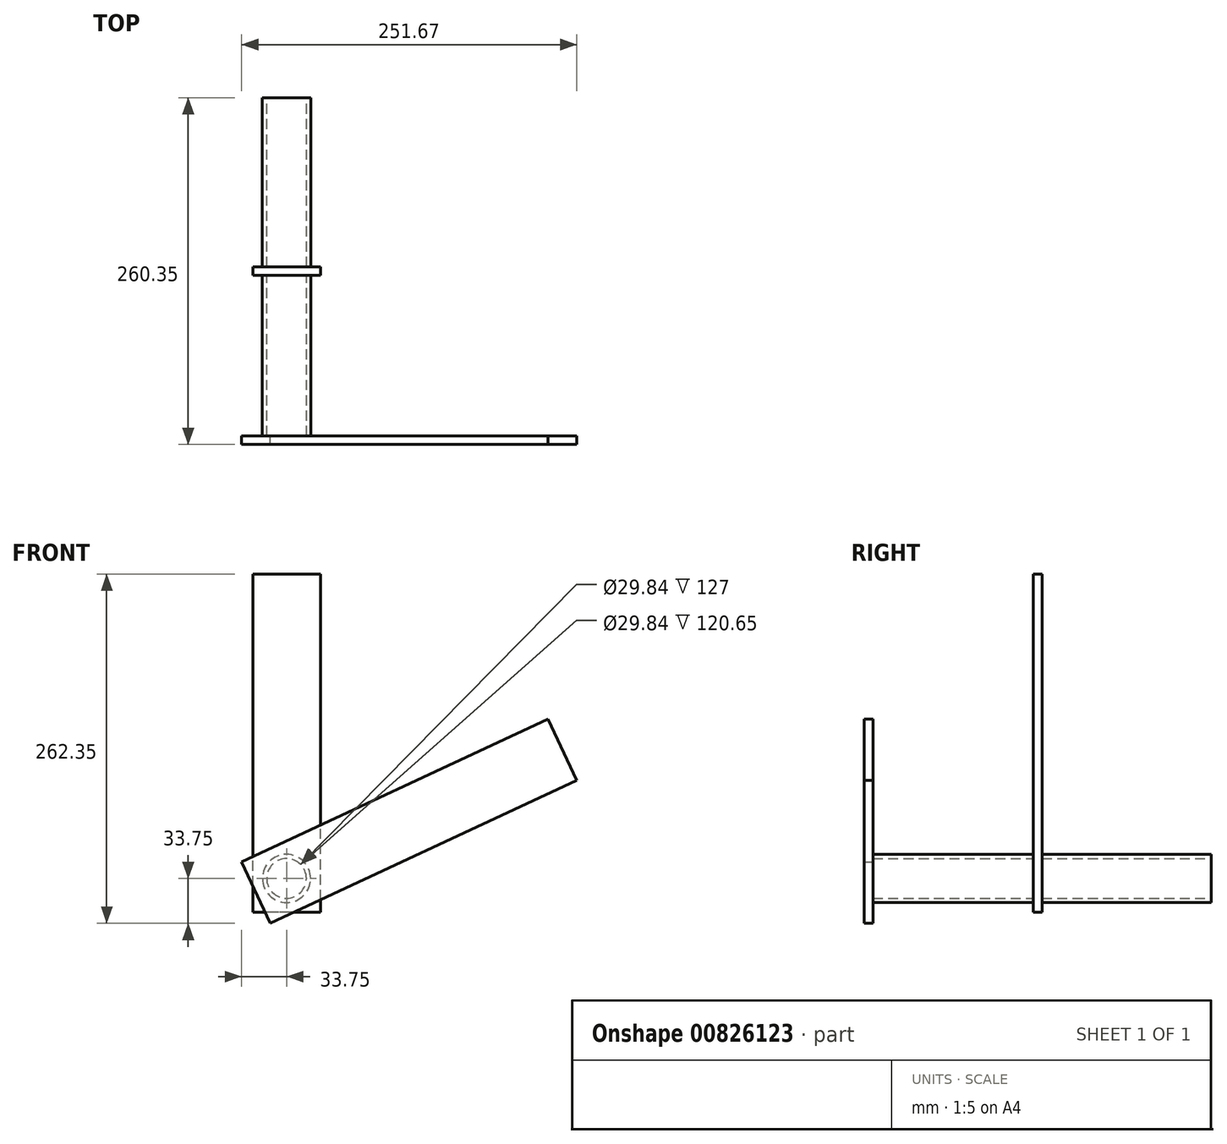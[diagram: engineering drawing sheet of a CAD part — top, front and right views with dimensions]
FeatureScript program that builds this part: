
annotation { "Feature Type Name" : "Feature", "Feature Type Description" : "" }
export const myFeature = defineFeature(function(context is Context, id is Id, definition is map)
    precondition{}
    {
        {
            var Q0;
            Q0=qCreatedBy(makeId("Front.planeOp"),FACE);
            var sketch = newSketch(context, id + "F0", { "sketchPlane" : qUnion([Q0])});
            skCircle(sketch, "E0", {"center": v(0, 0) * mm, "radius": 18.1 * mm});
            skCircle(sketch, "E1", {"center": v(0, 0) * mm, "radius": 14.92 * mm});
            skSolve(sketch);
        }
        {
            var Q0;
            Q0 = qSketchRegion(id + "F0", true);
            extrude(context, id + "F1", {"entities" : qUnion([Q0]), "endBound" : BoundingType.SYMMETRIC, "depth" : 254 * mm, "offsetDistance" : 25.4 * mm});
        }
        {
            var Q0;
            Q0=qCreatedBy(makeId("Front.planeOp"),FACE);
            var sketch = newSketch(context, id + "F2", { "sketchPlane" : qUnion([Q0])});
            skLineSegment(sketch, "E2", {"start": v(25.4, -25.4) * mm, "end": v(25.4, 228.6) * mm});
            skLineSegment(sketch, "E3", {"start": v(25.4, -25.4) * mm, "end": v(0, -25.4) * mm});
            skLineSegment(sketch, "E4", {"start": v(0, 37.04) * mm, "end": v(0, -46.45) * mm, "construction": true});
            skLineSegment(sketch, "E5", {"start": v(25.4, 228.6) * mm, "end": v(0, 228.6) * mm});
            skLineSegment(sketch, "E6.MirrorCS", {"start": v(-25.4, -25.4) * mm, "end": v(0, -25.4) * mm});
            skLineSegment(sketch, "E7.MirrorCS", {"start": v(-25.4, -25.4) * mm, "end": v(-25.4, 228.6) * mm});
            skLineSegment(sketch, "E8.MirrorCS", {"start": v(-25.4, 228.6) * mm, "end": v(0, 228.6) * mm});
            skSolve(sketch);
        }
        {
            var Q0;
            Q0 = qSketchRegion(id + "F2", true);
            extrude(context, id + "F3", {"entities" : qUnion([Q0]), "operationType" : NewBodyOperationType.ADD, "depth" : 6.35 * mm, "offsetDistance" : 25.4 * mm});
        }
        {
            var Q0;
            Q0=makeQuery(id+"F1.opExtrude","CAP_FACE",FACE,{"disambiguationData":[OSD([sQuery(id+"F0.wireOp",EDGE,"E0"),sQuery(id+"F0.wireOp",EDGE,"E1")])],"isStart":false});
            var sketch = newSketch(context, id + "F4", { "sketchPlane" : qUnion([Q0])});
            skLineSegment(sketch, "E9", {"start": v(0, 0) * mm, "end": v(207.18, 96.61) * mm, "construction": true});
            skLineSegment(sketch, "E10", {"start": v(207.18, 96.61) * mm, "end": v(217.92, 73.6) * mm});
            skLineSegment(sketch, "E11", {"start": v(217.92, 73.6) * mm, "end": v(-12.29, -33.75) * mm});
            skLineSegment(sketch, "E12.0", {"start": v(-23.02, -10.73) * mm, "end": v(-12.29, -33.75) * mm});
            skLineSegment(sketch, "E13", {"start": v(-23.02, -10.73) * mm, "end": v(0, 0) * mm, "construction": true});
            skLineSegment(sketch, "E14", {"start": v(207.18, 96.61) * mm, "end": v(0, 0) * mm, "construction": true});
            skLineSegment(sketch, "E15.MirrorCS", {"start": v(196.45, 119.63) * mm, "end": v(-33.75, 12.29) * mm});
            skLineSegment(sketch, "E16.MirrorCS", {"start": v(-23.02, -10.73) * mm, "end": v(-33.75, 12.29) * mm});
            skLineSegment(sketch, "E17.MirrorCS", {"start": v(207.18, 96.61) * mm, "end": v(196.45, 119.63) * mm});
            skSolve(sketch);
        }
        {
            var Q0;
            Q0 = qSketchRegion(id + "F4", true);
            extrude(context, id + "F5", {"entities" : qUnion([Q0]), "operationType" : NewBodyOperationType.ADD, "depth" : 6.35 * mm, "offsetDistance" : 25.4 * mm});
        }
    });
